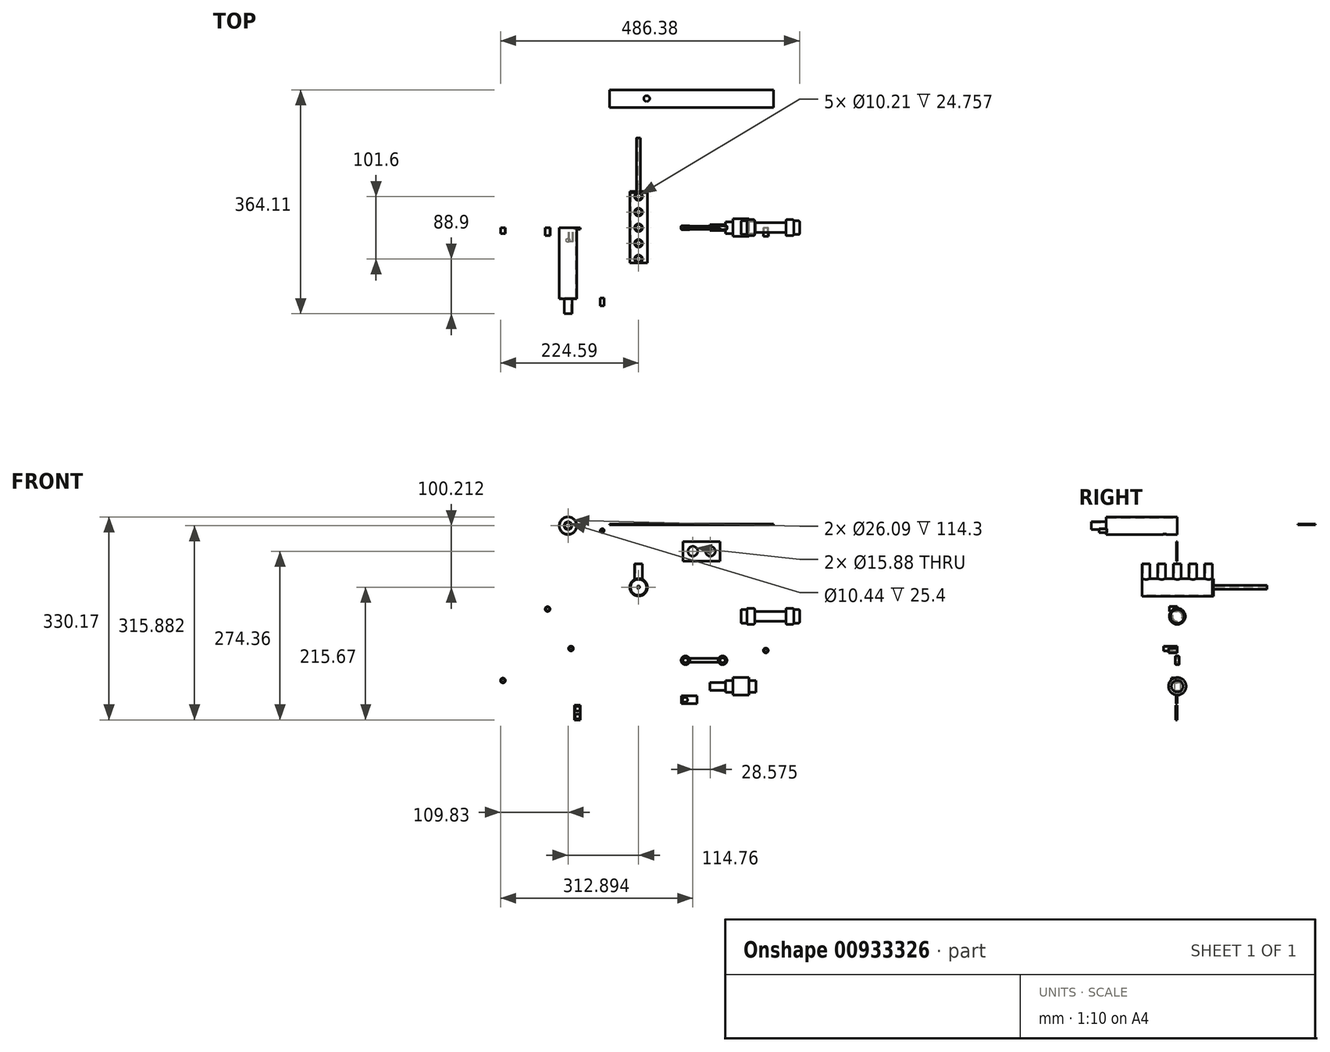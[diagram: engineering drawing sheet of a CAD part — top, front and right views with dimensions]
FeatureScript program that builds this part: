
annotation { "Feature Type Name" : "Feature", "Feature Type Description" : "" }
export const myFeature = defineFeature(function(context is Context, id is Id, definition is map)
    precondition{}
    {
        {
            var Q0;
            Q0=qCreatedBy(makeId("Front.planeOp"),FACE);
            var sketch = newSketch(context, id + "F0", { "sketchPlane" : qUnion([Q0])});
            skCircle(sketch, "E0", {"center": v(-114.76, 100.21) * mm, "radius": 14.29 * mm});
            skCircle(sketch, "E1", {"center": v(-114.76, 100.21) * mm, "radius": 13.04 * mm});
            skSolve(sketch);
        }
        {
            var Q0;
            Q0=makeQuery(id+"F0.imprint","IMPRINT",FACE,{"disambiguationData":[TD([[makeQuery(id+"F0.imprint","IMPRINT",EDGE,{"derivedFrom":sQuery(id+"F0.wireOp",EDGE,"E0")}),1.0]])]});
            extrude(context, id + "F1", {"entities" : qUnion([Q0]), "depth" : 114.3 * mm, "offsetDistance" : 25.4 * mm});
        }
        {
            var Q0;
            Q0=qCreatedBy(makeId("Front.planeOp"),FACE);
            var sketch = newSketch(context, id + "F2", { "sketchPlane" : qUnion([Q0])});
            skCircle(sketch, "E2", {"center": v(0, 0) * mm, "radius": 14.29 * mm});
            skSolve(sketch);
        }
        {
            var Q0;
            Q0=makeQuery(id+"F2.imprint","IMPRINT",FACE,{"disambiguationData":[TD([[makeQuery(id+"F2.imprint","IMPRINT",EDGE,{"derivedFrom":sQuery(id+"F2.wireOp",EDGE,"E2")}),1.0]])]});
            extrude(context, id + "F3", {"entities" : qUnion([Q0]), "depth" : 57.15 * mm, "offsetDistance" : 25.4 * mm});
        }
        {
            var Q0;
            Q0=makeQuery(id+"F3.opExtrude","CAP_FACE",FACE,{"disambiguationData":[OSD([sQuery(id+"F2.wireOp",EDGE,"E2")])],"isStart":true});
            extrude(context, id + "F4", {"entities" : qUnion([Q0]), "operationType" : NewBodyOperationType.ADD, "depth" : 57.15 * mm, "offsetDistance" : 25.4 * mm});
        }
        {
            var Q0;
            Q0=qCreatedBy(makeId("Top.planeOp"),FACE);
            var sketch = newSketch(context, id + "F5", { "sketchPlane" : qUnion([Q0])});
            skPoint(sketch, "E3", {"position": v(0, 50.8) * mm});
            skPoint(sketch, "E4", {"position": v(0, 25.4) * mm});
            skPoint(sketch, "E5", {"position": v(0, 0) * mm});
            skPoint(sketch, "E6", {"position": v(0, -25.4) * mm});
            skPoint(sketch, "E7", {"position": v(0, -50.8) * mm});
            skCircle(sketch, "E8", {"center": v(0, -50.8) * mm, "radius": 5.1 * mm});
            skCircle(sketch, "E9", {"center": v(0, -25.4) * mm, "radius": 5.1 * mm});
            skCircle(sketch, "E10", {"center": v(0, 0) * mm, "radius": 5.1 * mm});
            skCircle(sketch, "E11", {"center": v(0, 25.4) * mm, "radius": 5.1 * mm});
            skCircle(sketch, "E12", {"center": v(0, 50.8) * mm, "radius": 5.1 * mm});
            skCircle(sketch, "E13", {"center": v(0, -50.8) * mm, "radius": 6.35 * mm});
            skCircle(sketch, "E14", {"center": v(0, -25.4) * mm, "radius": 6.35 * mm});
            skCircle(sketch, "E15", {"center": v(0, 0) * mm, "radius": 6.35 * mm});
            skCircle(sketch, "E16", {"center": v(0, 25.4) * mm, "radius": 6.35 * mm});
            skCircle(sketch, "E17", {"center": v(0, 50.8) * mm, "radius": 6.35 * mm});
            skSolve(sketch);
        }
        {
            var Q0;
            Q0=makeQuery(id+"F5.imprint","IMPRINT",FACE,{"disambiguationData":[TD([[makeQuery(id+"F5.imprint","IMPRINT",EDGE,{"derivedFrom":sQuery(id+"F5.wireOp",EDGE,"E9")}),-1.0]])]});
            var Q1;
            Q1=makeQuery(id+"F5.imprint","IMPRINT",FACE,{"disambiguationData":[TD([[makeQuery(id+"F5.imprint","IMPRINT",EDGE,{"derivedFrom":sQuery(id+"F5.wireOp",EDGE,"E11")}),-1.0]])]});
            var Q2;
            Q2=makeQuery(id+"F5.imprint","IMPRINT",FACE,{"disambiguationData":[TD([[makeQuery(id+"F5.imprint","IMPRINT",EDGE,{"derivedFrom":sQuery(id+"F5.wireOp",EDGE,"E10")}),-1.0]])]});
            var Q3;
            Q3=makeQuery(id+"F5.imprint","IMPRINT",FACE,{"disambiguationData":[TD([[makeQuery(id+"F5.imprint","IMPRINT",EDGE,{"derivedFrom":sQuery(id+"F5.wireOp",EDGE,"E12")}),-1.0]])]});
            var Q4;
            Q4=makeQuery(id+"F5.imprint","IMPRINT",FACE,{"disambiguationData":[TD([[makeQuery(id+"F5.imprint","IMPRINT",EDGE,{"derivedFrom":sQuery(id+"F5.wireOp",EDGE,"E8")}),-1.0]])]});
            extrude(context, id + "F6", {"entities" : qUnion([Q0, Q1, Q2, Q3, Q4]), "operationType" : NewBodyOperationType.ADD, "depth" : 38.1 * mm, "offsetDistance" : 25.4 * mm});
        }
        {
            var Q0;
            Q0=makeQuery(id+"F3.opExtrude","CAP_FACE",FACE,{"disambiguationData":[OSD([sQuery(id+"F2.wireOp",EDGE,"E2")])],"isStart":false});
            var sketch = newSketch(context, id + "F7", { "sketchPlane" : qUnion([Q0])});
            skPoint(sketch, "E18", {"position": v(0, 0) * mm});
            skSolve(sketch);
        }
        {
            var Q0;
            Q0=sQuery(id+"F7.wireOp",VERTEX,"E18");
            var Q1;
            Q1=makeQuery(id+"F3.opExtrude","SWEPT_BODY",BODY,{"disambiguationData":[OSD([sQuery(id+"F2.wireOp",EDGE,"E2")])]});
            hole(context, id + "F8", {"style" : HoleStyle.SIMPLE, "endStyle" : HoleEndStyle.THROUGH, "holeDiameter" : 26.09 * mm, "majorDiameter" : 6.35 * mm, "isTappedThrough" : true, "tappedDepth" : 12.7 * mm, "tapClearance" : 3, "locations" : qUnion([Q0]), "scope" : qUnion([Q1])});
        }
        {
            var Q0;
            Q0=makeQuery(id+"F4.opExtrude","CAP_FACE",FACE,{"disambiguationData":[OSD([sQuery(id+"F2.wireOp",EDGE,"E2")])],"isStart":false});
            var sketch = newSketch(context, id + "F9", { "sketchPlane" : qUnion([Q0])});
            skCircle(sketch, "E19", {"center": v(0, 0) * mm, "radius": 14.29 * mm});
            skCircle(sketch, "E20", {"center": v(0, 0) * mm, "radius": 3.18 * mm});
            skCircle(sketch, "E21", {"center": v(0, 0) * mm, "radius": 1.59 * mm});
            skSolve(sketch);
        }
        {
            var Q0;
            Q0=makeQuery(id+"F9.imprint","IMPRINT",FACE,{"disambiguationData":[TD([[makeQuery(id+"F9.imprint","IMPRINT",EDGE,{"derivedFrom":sQuery(id+"F9.wireOp",EDGE,"E20")}),-1.0]])]});
            var Q1;
            Q1=makeQuery(id+"F9.imprint","IMPRINT",FACE,{"disambiguationData":[TD([[makeQuery(id+"F9.imprint","IMPRINT",EDGE,{"derivedFrom":sQuery(id+"F9.wireOp",EDGE,"E19")}),-1.0]])]});
            extrude(context, id + "F10", {"entities" : qUnion([Q0, Q1]), "depth" : 1.59 * mm, "offsetDistance" : 25.4 * mm});
        }
        {
            var Q0;
            Q0=makeQuery(id+"F9.imprint","IMPRINT",FACE,{"disambiguationData":[TD([[makeQuery(id+"F9.imprint","IMPRINT",EDGE,{"derivedFrom":sQuery(id+"F9.wireOp",EDGE,"E20")}),1.0]])]});
            extrude(context, id + "F11", {"entities" : qUnion([Q0]), "operationType" : NewBodyOperationType.ADD, "depth" : 88.9 * mm, "offsetDistance" : 25.4 * mm});
        }
        {
            var Q0;
            Q0=qCreatedBy(makeId("Top.planeOp"),FACE);
            cPlane(context, id + "F12", {"entities" : qUnion([Q0]), "cplaneType" : CPlaneType.OFFSET, "offset" : 101.6 * mm, "width" : 152.4 * mm, "height" : 152.4 * mm});
        }
        {
            var Q0;
            Q0=qCreatedBy(id+"F12.planeOp",FACE);
            var sketch = newSketch(context, id + "F13", { "sketchPlane" : qUnion([Q0])});
            skPoint(sketch, "E22", {"position": v(-114.8, -20.5) * mm});
            skSolve(sketch);
        }
        {
            var Q0;
            Q0=sQuery(id+"F13.wireOp",VERTEX,"E22");
            var Q1;
            Q1=makeQuery(id+"F1.opExtrude","SWEPT_BODY",BODY,{"disambiguationData":[OSD([sQuery(id+"F0.wireOp",EDGE,"E0"),sQuery(id+"F0.wireOp",EDGE,"E1")])]});
            hole(context, id + "F14", {"style" : HoleStyle.SIMPLE, "endStyle" : HoleEndStyle.THROUGH, "holeDiameter" : 6.35 * mm, "majorDiameter" : 6.35 * mm, "isTappedThrough" : true, "tappedDepth" : 12.7 * mm, "tapClearance" : 3, "locations" : qUnion([Q0]), "scope" : qUnion([Q1])});
        }
        {
            var Q0;
            Q0=makeQuery(id+"F1.opExtrude","CAP_FACE",FACE,{"disambiguationData":[OSD([sQuery(id+"F0.wireOp",EDGE,"E0"),sQuery(id+"F0.wireOp",EDGE,"E1")])],"isStart":false});
            var sketch = newSketch(context, id + "F15", { "sketchPlane" : qUnion([Q0])});
            skCircle(sketch, "E23", {"center": v(-114.76, 100.21) * mm, "radius": 14.29 * mm});
            skCircle(sketch, "E24", {"center": v(-114.76, 100.21) * mm, "radius": 6.35 * mm});
            skCircle(sketch, "E25", {"center": v(-114.76, 100.21) * mm, "radius": 5.22 * mm});
            skCircle(sketch, "E26", {"center": v(-59.07, 92.24) * mm, "radius": 3.18 * mm});
            skCircle(sketch, "E27", {"center": v(-59.07, 92.24) * mm, "radius": 2.38 * mm});
            skSolve(sketch);
        }
        {
            var Q0;
            Q0=makeQuery(id+"F15.imprint","IMPRINT",FACE,{"disambiguationData":[TD([[makeQuery(id+"F15.imprint","IMPRINT",EDGE,{"derivedFrom":sQuery(id+"F15.wireOp",EDGE,"E23")}),1.0]])]});
            var Q1;
            Q1=makeQuery(id+"F15.imprint","IMPRINT",FACE,{"disambiguationData":[TD([[makeQuery(id+"F15.imprint","IMPRINT",EDGE,{"derivedFrom":sQuery(id+"F15.wireOp",EDGE,"E24")}),-1.0]])]});
            extrude(context, id + "F16", {"entities" : qUnion([Q0, Q1]), "operationType" : NewBodyOperationType.ADD, "depth" : 1.59 * mm, "offsetDistance" : 25.4 * mm});
        }
        {
            var Q0;
            Q0=makeQuery(id+"F15.imprint","IMPRINT",FACE,{"disambiguationData":[TD([[makeQuery(id+"F15.imprint","IMPRINT",EDGE,{"derivedFrom":sQuery(id+"F15.wireOp",EDGE,"E24")}),1.0]])]});
            extrude(context, id + "F17", {"entities" : qUnion([Q0]), "operationType" : NewBodyOperationType.ADD, "depth" : 25.4 * mm, "offsetDistance" : 25.4 * mm});
        }
        {
            var Q0;
            Q0=makeQuery(id+"F15.imprint","IMPRINT",FACE,{"disambiguationData":[TD([[makeQuery(id+"F15.imprint","IMPRINT",EDGE,{"derivedFrom":sQuery(id+"F15.wireOp",EDGE,"E26")}),1.0]])]});
            extrude(context, id + "F18", {"entities" : qUnion([Q0]), "depth" : 12.7 * mm, "offsetDistance" : 25.4 * mm});
        }
        {
            var Q0;
            Q0=qCreatedBy(makeId("Front.planeOp"),FACE);
            var sketch = newSketch(context, id + "F19", { "sketchPlane" : qUnion([Q0])});
            skLineSegment(sketch, "E28.bottom", {"start": v(72.43, 42.82) * mm, "end": v(132.75, 42.82) * mm});
            skLineSegment(sketch, "E28.top", {"start": v(72.43, 74.57) * mm, "end": v(132.75, 74.57) * mm});
            skLineSegment(sketch, "E28.left", {"start": v(72.43, 42.82) * mm, "end": v(72.43, 74.57) * mm});
            skLineSegment(sketch, "E28.right", {"start": v(132.75, 42.82) * mm, "end": v(132.75, 74.57) * mm});
            skCircle(sketch, "E29", {"center": v(88.3, 58.7) * mm, "radius": 7.94 * mm});
            skCircle(sketch, "E30", {"center": v(116.88, 58.7) * mm, "radius": 7.94 * mm});
            skSolve(sketch);
        }
        {
            var Q0;
            Q0=makeQuery(id+"F19.imprint","IMPRINT",FACE,{"disambiguationData":[TD([[makeQuery(id+"F19.imprint","IMPRINT",EDGE,{"derivedFrom":sQuery(id+"F19.wireOp",EDGE,"E28.bottom")}),1.0]])]});
            extrude(context, id + "F20", {"entities" : qUnion([Q0]), "depth" : 1.59 * mm, "offsetDistance" : 25.4 * mm});
        }
        {
            var Q0;
            Q0=qCreatedBy(makeId("Front.planeOp"),FACE);
            var sketch = newSketch(context, id + "F21", { "sketchPlane" : qUnion([Q0])});
            skLineSegment(sketch, "E31", {"start": v(303.18, -47.23) * mm, "end": v(150.78, -47.23) * mm, "construction": true});
            skLineSegment(sketch, "E32.bottom", {"start": v(176.06, -58.34) * mm, "end": v(166.54, -58.34) * mm});
            skLineSegment(sketch, "E32.top", {"start": v(176.06, -36.11) * mm, "end": v(166.54, -36.11) * mm});
            skLineSegment(sketch, "E32.left", {"start": v(176.06, -58.34) * mm, "end": v(176.06, -36.11) * mm});
            skLineSegment(sketch, "E32.right", {"start": v(166.54, -58.34) * mm, "end": v(166.54, -36.11) * mm});
            skPoint(sketch, "E32.middle", {"position": v(171.3, -47.23) * mm});
            skLineSegment(sketch, "E33.bottom", {"start": v(188.76, -60.27) * mm, "end": v(176.06, -60.27) * mm});
            skLineSegment(sketch, "E33.top", {"start": v(188.76, -34.18) * mm, "end": v(176.06, -34.18) * mm});
            skLineSegment(sketch, "E33.left", {"start": v(188.76, -60.27) * mm, "end": v(188.76, -34.18) * mm});
            skLineSegment(sketch, "E33.right", {"start": v(176.06, -60.27) * mm, "end": v(176.06, -34.18) * mm});
            skPoint(sketch, "E33.middle", {"position": v(182.41, -47.23) * mm});
            skLineSegment(sketch, "E34.bottom", {"start": v(239.56, -55.16) * mm, "end": v(188.76, -55.16) * mm});
            skLineSegment(sketch, "E34.top", {"start": v(239.56, -39.29) * mm, "end": v(188.76, -39.29) * mm});
            skLineSegment(sketch, "E34.left", {"start": v(239.56, -55.16) * mm, "end": v(239.56, -39.29) * mm});
            skLineSegment(sketch, "E34.right", {"start": v(188.76, -55.16) * mm, "end": v(188.76, -39.29) * mm});
            skPoint(sketch, "E34.middle", {"position": v(214.16, -47.23) * mm});
            skLineSegment(sketch, "E35.bottom", {"start": v(252.26, -60.27) * mm, "end": v(239.56, -60.27) * mm});
            skLineSegment(sketch, "E35.top", {"start": v(252.26, -34.18) * mm, "end": v(239.56, -34.18) * mm});
            skLineSegment(sketch, "E35.left", {"start": v(252.26, -60.27) * mm, "end": v(252.26, -34.18) * mm});
            skLineSegment(sketch, "E35.right", {"start": v(239.56, -60.27) * mm, "end": v(239.56, -34.18) * mm});
            skPoint(sketch, "E35.middle", {"position": v(245.91, -47.23) * mm});
            skLineSegment(sketch, "E36.bottom", {"start": v(261.79, -58.34) * mm, "end": v(252.26, -58.34) * mm});
            skLineSegment(sketch, "E36.top", {"start": v(261.79, -36.11) * mm, "end": v(252.26, -36.11) * mm});
            skLineSegment(sketch, "E36.left", {"start": v(261.79, -58.34) * mm, "end": v(261.79, -36.11) * mm});
            skLineSegment(sketch, "E36.right", {"start": v(252.26, -58.34) * mm, "end": v(252.26, -36.11) * mm});
            skPoint(sketch, "E36.middle", {"position": v(257.03, -47.23) * mm});
            skLineSegment(sketch, "E37", {"start": v(166.54, -47.23) * mm, "end": v(261.79, -47.23) * mm});
            skSolve(sketch);
        }
        {
            var Q0;
            {var subQ0=sQuery(id+"F21.wireOp",EDGE,"E32.top");Q0=makeQuery(id+"F21.imprint","IMPRINT",FACE,{"disambiguationData":[TD([[makeQuery(id+"F21.imprint","IMPRINT",EDGE,{"derivedFrom":subQ0}),1.0]])]});}
            var Q1;
            {var subQ3=sQuery(id+"F21.wireOp",EDGE,"E34.top");Q1=makeQuery(id+"F21.imprint","IMPRINT",FACE,{"disambiguationData":[TD([[makeQuery(id+"F21.imprint","IMPRINT",EDGE,{"derivedFrom":subQ3}),1.0]])]});}
            var Q2;
            {var subQ1=sQuery(id+"F21.wireOp",EDGE,"E35.top");Q2=makeQuery(id+"F21.imprint","IMPRINT",FACE,{"disambiguationData":[TD([[makeQuery(id+"F21.imprint","IMPRINT",EDGE,{"derivedFrom":subQ1}),1.0]])]});}
            var Q3;
            {var subQ3=sQuery(id+"F21.wireOp",EDGE,"E36.top");Q3=makeQuery(id+"F21.imprint","IMPRINT",FACE,{"disambiguationData":[TD([[makeQuery(id+"F21.imprint","IMPRINT",EDGE,{"derivedFrom":subQ3}),1.0]])]});}
            var Q4;
            {var subQ1=sQuery(id+"F21.wireOp",EDGE,"E33.top");Q4=makeQuery(id+"F21.imprint","IMPRINT",FACE,{"disambiguationData":[TD([[makeQuery(id+"F21.imprint","IMPRINT",EDGE,{"derivedFrom":subQ1}),1.0]])]});}
            var Q5;
            Q5=sQuery(id+"F21.wireOp",EDGE,"E31");
            revolve(context, id + "F22", {"surfaceOperationType" : NewSurfaceOperationType.NEW, "entities" : qUnion([Q0, Q1, Q2, Q3, Q4]), "axis" : qUnion([Q5]), "revolveType" : RevolveType.FULL});
        }
        {
            var Q0;
            Q0=makeQuery(id+"F22.opRevolve","SWEPT_FACE",FACE,{"disambiguationData":[OSD([sQuery(id+"F21.wireOp",EDGE,"E33.top")])]});
            var Q1;
            Q1=makeQuery(id+"F22.opRevolve","SWEPT_FACE",FACE,{"disambiguationData":[OSD([sQuery(id+"F21.wireOp",EDGE,"E32.right")])]});
            var Q2;
            Q2=makeQuery(id+"F22.opRevolve","SWEPT_FACE",FACE,{"disambiguationData":[OSD([sQuery(id+"F21.wireOp",EDGE,"E36.left")])]});
            var Q3;
            Q3=makeQuery(id+"F22.opRevolve","SWEPT_FACE",FACE,{"disambiguationData":[OSD([sQuery(id+"F21.wireOp",EDGE,"E35.top")])]});
            fillet(context, id + "F23", {"entities" : qUnion([Q0, Q1, Q2, Q3]), "tangentPropagation" : true, "radius" : 1.59 * mm, "defaultsChanged" : false, "vertexSettings" : [], "allowEdgeOverflow" : false});
        }
        {
            var Q0;
            Q0=qCreatedBy(makeId("Front.planeOp"),FACE);
            var sketch = newSketch(context, id + "F24", { "sketchPlane" : qUnion([Q0])});
            skCircle(sketch, "E38", {"center": v(-147.92, -35.36) * mm, "radius": 2.72 * mm});
            skCircle(sketch, "E39", {"center": v(-147.92, -35.36) * mm, "radius": 3.97 * mm});
            skCircle(sketch, "E40", {"center": v(-109.92, -99.64) * mm, "radius": 2.72 * mm});
            skCircle(sketch, "E41", {"center": v(-109.92, -99.64) * mm, "radius": 3.97 * mm});
            skCircle(sketch, "E42", {"center": v(-220.62, -151.58) * mm, "radius": 3.97 * mm});
            skCircle(sketch, "E43", {"center": v(-220.62, -151.58) * mm, "radius": 2.72 * mm});
            skLineSegment(sketch, "E44.bottom", {"start": v(-94.58, -215.67) * mm, "end": v(-104.18, -215.67) * mm});
            skLineSegment(sketch, "E44.top", {"start": v(-94.58, -191.86) * mm, "end": v(-104.18, -191.86) * mm});
            skLineSegment(sketch, "E44.left", {"start": v(-94.58, -215.67) * mm, "end": v(-94.58, -191.86) * mm});
            skLineSegment(sketch, "E44.right", {"start": v(-104.18, -215.67) * mm, "end": v(-104.18, -191.86) * mm});
            skPoint(sketch, "E44.middle", {"position": v(-99.38, -203.76) * mm});
            skCircle(sketch, "E45", {"center": v(-99.37, -197.41) * mm, "radius": 3.97 * mm});
            skCircle(sketch, "E46", {"center": v(-99.38, -210.11) * mm, "radius": 3.97 * mm});
            skPoint(sketch, "E46.centerSnap0", {"position": v(-99.38, -215.67) * mm});
            skSolve(sketch);
        }
        {
            var Q0;
            Q0=makeQuery(id+"F24.imprint","IMPRINT",FACE,{"disambiguationData":[TD([[makeQuery(id+"F24.imprint","IMPRINT",EDGE,{"derivedFrom":sQuery(id+"F24.wireOp",EDGE,"E44.bottom")}),-1.0]])]});
            extrude(context, id + "F25", {"entities" : qUnion([Q0]), "depth" : 2.78 * mm, "offsetDistance" : 25.4 * mm});
        }
        {
            var Q0;
            Q0=makeQuery(id+"F24.imprint","IMPRINT",FACE,{"disambiguationData":[TD([[makeQuery(id+"F24.imprint","IMPRINT",EDGE,{"derivedFrom":sQuery(id+"F24.wireOp",EDGE,"E38")}),-1.0]])]});
            extrude(context, id + "F26", {"entities" : qUnion([Q0]), "depth" : 12.7 * mm, "offsetDistance" : 25.4 * mm});
        }
        {
            var Q0;
            Q0=makeQuery(id+"F24.imprint","IMPRINT",FACE,{"disambiguationData":[TD([[makeQuery(id+"F24.imprint","IMPRINT",EDGE,{"derivedFrom":sQuery(id+"F24.wireOp",EDGE,"E42")}),1.0]])]});
            extrude(context, id + "F27", {"entities" : qUnion([Q0]), "depth" : 9.52 * mm, "offsetDistance" : 25.4 * mm});
        }
        {
            var Q0;
            Q0=makeQuery(id+"F24.imprint","IMPRINT",FACE,{"disambiguationData":[TD([[makeQuery(id+"F24.imprint","IMPRINT",EDGE,{"derivedFrom":sQuery(id+"F24.wireOp",EDGE,"E40")}),-1.0]])]});
            extrude(context, id + "F28", {"entities" : qUnion([Q0]), "depth" : 22.22 * mm, "offsetDistance" : 25.4 * mm});
        }
        {
            var Q0;
            Q0=qCreatedBy(makeId("Front.planeOp"),FACE);
            var sketch = newSketch(context, id + "F29", { "sketchPlane" : qUnion([Q0])});
            skCircle(sketch, "E47", {"center": v(76.32, -118.8) * mm, "radius": 3.97 * mm});
            skCircle(sketch, "E48", {"center": v(76.32, -118.8) * mm, "radius": 7.14 * mm});
            skCircle(sketch, "E49", {"center": v(136.65, -118.8) * mm, "radius": 3.97 * mm});
            skCircle(sketch, "E50", {"center": v(136.65, -118.8) * mm, "radius": 7.14 * mm});
            skLineSegment(sketch, "E51.bottom", {"start": v(82.72, -121.98) * mm, "end": v(130.25, -121.98) * mm});
            skLineSegment(sketch, "E51.top", {"start": v(82.72, -115.63) * mm, "end": v(130.25, -115.63) * mm});
            skLineSegment(sketch, "E52.bottom", {"start": v(69.68, -176.7) * mm, "end": v(95.08, -176.7) * mm});
            skLineSegment(sketch, "E52.top", {"start": v(69.68, -189.4) * mm, "end": v(95.08, -189.4) * mm});
            skLineSegment(sketch, "E52.left", {"start": v(69.68, -176.7) * mm, "end": v(69.68, -189.4) * mm});
            skLineSegment(sketch, "E52.right", {"start": v(95.08, -176.7) * mm, "end": v(95.08, -189.4) * mm});
            skCircle(sketch, "E53", {"center": v(75.68, -183.04) * mm, "radius": 3.97 * mm});
            skPoint(sketch, "E53.centerSnap0", {"position": v(69.68, -183.04) * mm});
            skLineSegment(sketch, "E54.bottom", {"start": v(116.06, -154.65) * mm, "end": v(141.46, -154.65) * mm});
            skLineSegment(sketch, "E54.top", {"start": v(116.06, -167.35) * mm, "end": v(141.46, -167.35) * mm});
            skLineSegment(sketch, "E54.left", {"start": v(116.06, -154.65) * mm, "end": v(116.06, -167.35) * mm});
            skLineSegment(sketch, "E54.right", {"start": v(141.46, -154.65) * mm, "end": v(141.46, -167.35) * mm});
            skLineSegment(sketch, "E55.bottom", {"start": v(141.46, -151.47) * mm, "end": v(153.46, -151.47) * mm});
            skLineSegment(sketch, "E55.top", {"start": v(141.46, -170.52) * mm, "end": v(153.46, -170.52) * mm});
            skLineSegment(sketch, "E55.left", {"start": v(141.46, -151.47) * mm, "end": v(141.46, -170.52) * mm});
            skLineSegment(sketch, "E55.right", {"start": v(153.46, -151.47) * mm, "end": v(153.46, -170.52) * mm});
            skLineSegment(sketch, "E56", {"start": v(116.06, -161) * mm, "end": v(225.74, -161) * mm, "construction": true});
            skLineSegment(sketch, "E57.bottom", {"start": v(153.46, -146.71) * mm, "end": v(179.37, -146.71) * mm});
            skLineSegment(sketch, "E57.top", {"start": v(153.46, -175.29) * mm, "end": v(179.37, -175.29) * mm});
            skLineSegment(sketch, "E57.left", {"start": v(153.46, -146.71) * mm, "end": v(153.46, -175.29) * mm});
            skLineSegment(sketch, "E57.right", {"start": v(179.37, -146.71) * mm, "end": v(179.37, -175.29) * mm});
            skLineSegment(sketch, "E58.bottom", {"start": v(179.37, -151.47) * mm, "end": v(190.88, -151.47) * mm});
            skLineSegment(sketch, "E58.top", {"start": v(179.37, -170.52) * mm, "end": v(190.88, -170.52) * mm});
            skLineSegment(sketch, "E58.left", {"start": v(179.37, -151.47) * mm, "end": v(179.37, -170.52) * mm});
            skLineSegment(sketch, "E58.right", {"start": v(190.88, -151.47) * mm, "end": v(190.88, -170.52) * mm});
            skLineSegment(sketch, "E59", {"start": v(141.46, -161) * mm, "end": v(190.88, -161) * mm});
            skCircle(sketch, "E60", {"center": v(207.02, -102.74) * mm, "radius": 3.97 * mm});
            skCircle(sketch, "E61", {"center": v(207.02, -102.74) * mm, "radius": 2.73 * mm});
            skSolve(sketch);
        }
        {
            var Q0;
            {var subQ3=sQuery(id+"F29.wireOp",EDGE,"E55.bottom");Q0=makeQuery(id+"F29.imprint","IMPRINT",FACE,{"disambiguationData":[TD([[makeQuery(id+"F29.imprint","IMPRINT",EDGE,{"derivedFrom":subQ3}),-1.0]])]});}
            var Q1;
            {var subQ3=sQuery(id+"F29.wireOp",EDGE,"E58.bottom");Q1=makeQuery(id+"F29.imprint","IMPRINT",FACE,{"disambiguationData":[TD([[makeQuery(id+"F29.imprint","IMPRINT",EDGE,{"derivedFrom":subQ3}),-1.0]])]});}
            var Q2;
            {var subQ3=sQuery(id+"F29.wireOp",EDGE,"E57.bottom");Q2=makeQuery(id+"F29.imprint","IMPRINT",FACE,{"disambiguationData":[TD([[makeQuery(id+"F29.imprint","IMPRINT",EDGE,{"derivedFrom":subQ3}),-1.0]])]});}
            var Q3;
            Q3=sQuery(id+"F29.wireOp",EDGE,"E56");
            revolve(context, id + "F30", {"surfaceOperationType" : NewSurfaceOperationType.NEW, "entities" : qUnion([Q0, Q1, Q2]), "axis" : qUnion([Q3]), "revolveType" : RevolveType.FULL});
        }
        {
            var Q0;
            {var subQ4=sQuery(id+"F29.wireOp",EDGE,"E54.bottom");Q0=makeQuery(id+"F29.imprint","IMPRINT",FACE,{"disambiguationData":[TD([[makeQuery(id+"F29.imprint","IMPRINT",EDGE,{"derivedFrom":subQ4}),-1.0]])]});}
            extrude(context, id + "F31", {"entities" : qUnion([Q0]), "operationType" : NewBodyOperationType.ADD, "depth" : 4.76 * mm, "offsetDistance" : 25.4 * mm});
        }
        {
            var Q0;
            {var subQ4=sQuery(id+"F29.wireOp",EDGE,"E54.bottom");Q0=makeQuery(id+"F29.imprint","IMPRINT",FACE,{"disambiguationData":[TD([[makeQuery(id+"F29.imprint","IMPRINT",EDGE,{"derivedFrom":subQ4}),-1.0]])]});}
            extrude(context, id + "F32", {"entities" : qUnion([Q0]), "operationType" : NewBodyOperationType.ADD, "oppositeDirection" : true, "depth" : 4.76 * mm, "offsetDistance" : 25.4 * mm});
        }
        {
            var Q0;
            Q0=makeQuery(id+"F29.imprint","IMPRINT",FACE,{"disambiguationData":[TD([[makeQuery(id+"F29.imprint","IMPRINT",EDGE,{"derivedFrom":sQuery(id+"F29.wireOp",EDGE,"E52.bottom")}),-1.0]])]});
            extrude(context, id + "F33", {"entities" : qUnion([Q0]), "depth" : 2.38 * mm, "offsetDistance" : 25.4 * mm});
        }
        {
            var Q0;
            {var subQ0=sQuery(id+"F29.wireOp",EDGE,"E51.bottom");Q0=makeQuery(id+"F29.imprint","IMPRINT",FACE,{"disambiguationData":[TD([[makeQuery(id+"F29.imprint","IMPRINT",EDGE,{"derivedFrom":subQ0}),1.0]])]});}
            extrude(context, id + "F34", {"entities" : qUnion([Q0]), "depth" : 2.38 * mm, "offsetDistance" : 25.4 * mm});
        }
        {
            var Q0;
            {var subQ0=sQuery(id+"F29.wireOp",EDGE,"E51.bottom");Q0=makeQuery(id+"F29.imprint","IMPRINT",FACE,{"disambiguationData":[TD([[makeQuery(id+"F29.imprint","IMPRINT",EDGE,{"derivedFrom":subQ0}),1.0]])]});}
            extrude(context, id + "F35", {"entities" : qUnion([Q0]), "operationType" : NewBodyOperationType.ADD, "oppositeDirection" : true, "depth" : 2.38 * mm, "offsetDistance" : 25.4 * mm});
        }
        {
            var Q0;
            Q0=makeQuery(id+"F29.imprint","IMPRINT",FACE,{"disambiguationData":[TD([[makeQuery(id+"F29.imprint","IMPRINT",EDGE,{"derivedFrom":sQuery(id+"F29.wireOp",EDGE,"E47")}),-1.0]])]});
            var Q1;
            Q1=makeQuery(id+"F29.imprint","IMPRINT",FACE,{"disambiguationData":[TD([[makeQuery(id+"F29.imprint","IMPRINT",EDGE,{"derivedFrom":sQuery(id+"F29.wireOp",EDGE,"E49")}),-1.0]])]});
            extrude(context, id + "F36", {"entities" : qUnion([Q0, Q1]), "operationType" : NewBodyOperationType.ADD, "depth" : 3.17 * mm, "offsetDistance" : 25.4 * mm});
        }
        {
            var Q0;
            Q0=makeQuery(id+"F29.imprint","IMPRINT",FACE,{"disambiguationData":[TD([[makeQuery(id+"F29.imprint","IMPRINT",EDGE,{"derivedFrom":sQuery(id+"F29.wireOp",EDGE,"E47")}),-1.0]])]});
            var Q1;
            Q1=makeQuery(id+"F29.imprint","IMPRINT",FACE,{"disambiguationData":[TD([[makeQuery(id+"F29.imprint","IMPRINT",EDGE,{"derivedFrom":sQuery(id+"F29.wireOp",EDGE,"E49")}),-1.0]])]});
            extrude(context, id + "F37", {"entities" : qUnion([Q0, Q1]), "operationType" : NewBodyOperationType.ADD, "oppositeDirection" : true, "depth" : 3.17 * mm, "offsetDistance" : 25.4 * mm});
        }
        {
            var Q0;
            Q0=makeQuery(id+"F34.opExtrude","CAP_EDGE",EDGE,{"disambiguationData":[OSD([sQuery(id+"F29.wireOp",EDGE,"E51.top")])],"isStart":false});
            var Q1;
            Q1=makeQuery(id+"F34.opExtrude","CAP_EDGE",EDGE,{"disambiguationData":[OSD([sQuery(id+"F29.wireOp",EDGE,"E51.bottom")])],"isStart":false});
            var Q2;
            Q2=makeQuery(id+"F35.opExtrude","CAP_EDGE",EDGE,{"disambiguationData":[OSD([sQuery(id+"F29.wireOp",EDGE,"E51.top")])],"isStart":false});
            var Q3;
            Q3=makeQuery(id+"F35.opExtrude","CAP_EDGE",EDGE,{"disambiguationData":[OSD([sQuery(id+"F29.wireOp",EDGE,"E51.bottom")])],"isStart":false});
            fillet(context, id + "F38", {"entities" : qUnion([Q0, Q1, Q2, Q3]), "tangentPropagation" : true, "radius" : 3.17 * mm, "defaultsChanged" : false, "vertexSettings" : [], "allowEdgeOverflow" : false});
        }
        {
            var Q0;
            Q0=makeQuery(id+"F37.opExtrude","CAP_EDGE",EDGE,{"disambiguationData":[OSD([sQuery(id+"F29.wireOp",EDGE,"E48")])],"isStart":false});
            var Q1;
            Q1=makeQuery(id+"F36.opExtrude","CAP_EDGE",EDGE,{"disambiguationData":[OSD([sQuery(id+"F29.wireOp",EDGE,"E48")])],"isStart":false});
            var Q2;
            Q2=makeQuery(id+"F36.opExtrude","CAP_EDGE",EDGE,{"disambiguationData":[OSD([sQuery(id+"F29.wireOp",EDGE,"E50")])],"isStart":false});
            var Q3;
            Q3=makeQuery(id+"F37.opExtrude","CAP_EDGE",EDGE,{"disambiguationData":[OSD([sQuery(id+"F29.wireOp",EDGE,"E50")])],"isStart":false});
            fillet(context, id + "F39", {"entities" : qUnion([Q0, Q1, Q2, Q3]), "tangentPropagation" : true, "radius" : 1.59 * mm, "defaultsChanged" : false, "vertexSettings" : [], "allowEdgeOverflow" : false});
        }
        {
            var Q0;
            Q0=makeQuery(id+"F29.imprint","IMPRINT",FACE,{"disambiguationData":[TD([[makeQuery(id+"F29.imprint","IMPRINT",EDGE,{"derivedFrom":sQuery(id+"F29.wireOp",EDGE,"E60")}),1.0]])]});
            extrude(context, id + "F40", {"entities" : qUnion([Q0]), "depth" : 14.29 * mm, "offsetDistance" : 25.4 * mm});
        }
        {
            var Q0;
            Q0=qCreatedBy(id+"F12.planeOp",FACE);
            var sketch = newSketch(context, id + "F41", { "sketchPlane" : qUnion([Q0])});
            skLineSegment(sketch, "E62.bottom", {"start": v(219.67, 195.83) * mm, "end": v(-47.03, 195.83) * mm});
            skLineSegment(sketch, "E62.top", {"start": v(219.67, 224.4) * mm, "end": v(-47.03, 224.4) * mm});
            skLineSegment(sketch, "E62.left", {"start": v(219.67, 195.83) * mm, "end": v(219.67, 224.4) * mm});
            skLineSegment(sketch, "E62.right", {"start": v(-47.03, 195.83) * mm, "end": v(-47.03, 224.4) * mm});
            skPoint(sketch, "E62.middle", {"position": v(86.32, 210.12) * mm});
            skCircle(sketch, "E63", {"center": v(13.3, 210.12) * mm, "radius": 4.76 * mm});
            skSolve(sketch);
        }
        {
            var Q0;
            Q0=makeQuery(id+"F41.imprint","IMPRINT",FACE,{"disambiguationData":[TD([[makeQuery(id+"F41.imprint","IMPRINT",EDGE,{"derivedFrom":sQuery(id+"F41.wireOp",EDGE,"E62.bottom")}),-1.0]])]});
            extrude(context, id + "F42", {"entities" : qUnion([Q0]), "depth" : 1.59 * mm, "offsetDistance" : 25.4 * mm});
        }
    });
